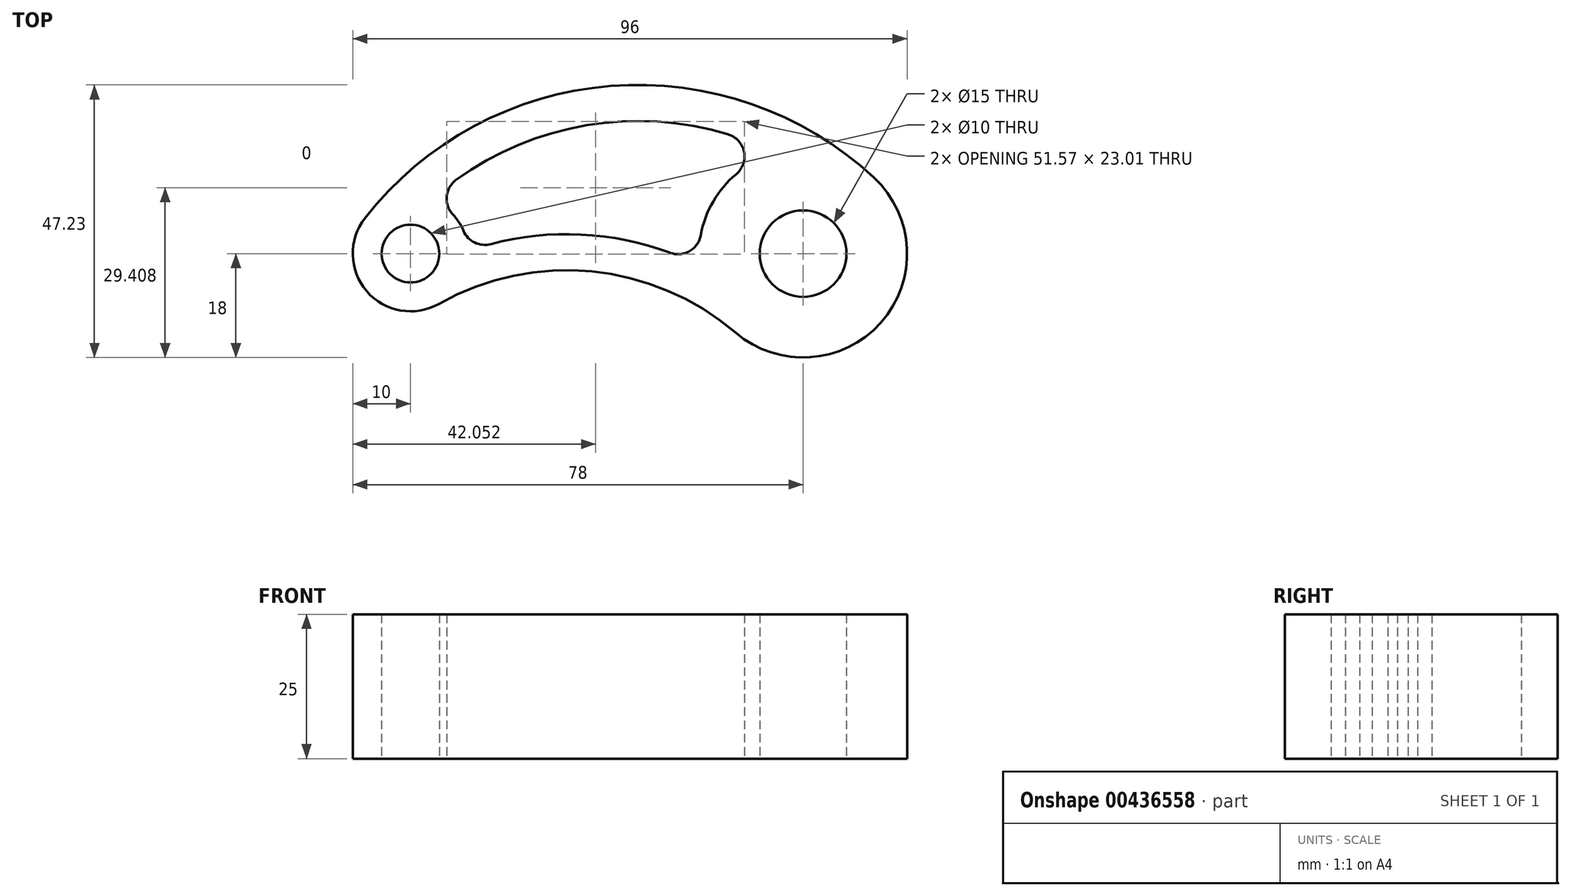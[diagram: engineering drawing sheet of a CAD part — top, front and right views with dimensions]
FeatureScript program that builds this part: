
annotation { "Feature Type Name" : "Feature", "Feature Type Description" : "" }
export const myFeature = defineFeature(function(context is Context, id is Id, definition is map)
    precondition{}
    {
        {
            var Q0;
            Q0=qCreatedBy(makeId("Top.planeOp"),FACE);
            var sketch = newSketch(context, id + "F0", { "sketchPlane" : qUnion([Q0])});
            skCircle(sketch, "E0", {"center": v(68, 0) * mm, "radius": 7.5 * mm});
            skArc(sketch, "E1", {"start": v(80.25, 13.19) * mm, "mid": v(81.44, -11.98) * mm, "end": v(56.3, -13.68) * mm});
            skCircle(sketch, "E2", {"center": v(0, 0) * mm, "radius": 5 * mm});
            skArc(sketch, "E3", {"start": v(-7.88, 6.15) * mm, "mid": v(-7.58, -6.53) * mm, "end": v(4.92, -8.7) * mm});
            skArc(sketch, "E4", {"start": v(56.3, -13.68) * mm, "mid": v(31.4, -3.1) * mm, "end": v(4.92, -8.7) * mm});
            skArc(sketch, "E5", {"start": v(80.25, 13.19) * mm, "mid": v(34.64, 29.04) * mm, "end": v(-7.88, 6.15) * mm});
            skArc(sketch, "E6", {"start": v(13.9, 1.65) * mm, "mid": v(29.54, 3.3) * mm, "end": v(44.95, 0.14) * mm});
            skArc(sketch, "E7", {"start": v(7.9, 12.78) * mm, "mid": v(30.53, 22.24) * mm, "end": v(55, 20.67) * mm});
            skArc(sketch, "E8", {"start": v(7.32, 6.81) * mm, "mid": v(8.38, 5.46) * mm, "end": v(9.2, 3.94) * mm});
            skArc(sketch, "E9", {"start": v(56.42, 13.78) * mm, "mid": v(52.42, 9.02) * mm, "end": v(50.28, 3.18) * mm});
            skPoint(sketch, "E10.visualSharp", {"position": v(10, 0.44) * mm});
            skArc(sketch, "E10.filletArc", {"start": v(9.2, 3.94) * mm, "mid": v(11.12, 1.92) * mm, "end": v(13.9, 1.65) * mm});
            skPoint(sketch, "E11.visualSharp", {"position": v(3.61, 9.32) * mm});
            skArc(sketch, "E11.filletArc", {"start": v(7.9, 12.78) * mm, "mid": v(6.27, 9.93) * mm, "end": v(7.32, 6.81) * mm});
            skPoint(sketch, "E12.visualSharp", {"position": v(63.3, 17.38) * mm});
            skArc(sketch, "E12.filletArc", {"start": v(56.42, 13.78) * mm, "mid": v(57.76, 17.65) * mm, "end": v(55, 20.67) * mm});
            skPoint(sketch, "E13.visualSharp", {"position": v(50.12, -2.12) * mm});
            skArc(sketch, "E13.filletArc", {"start": v(44.95, 0.14) * mm, "mid": v(48.33, 0.42) * mm, "end": v(50.28, 3.18) * mm});
            skSolve(sketch);
        }
        {
            var Q0;
            Q0=makeQuery(id+"F0.imprint","IMPRINT",FACE,{"disambiguationData":[TD([[makeQuery(id+"F0.imprint","IMPRINT",EDGE,{"derivedFrom":sQuery(id+"F0.wireOp",EDGE,"E0")}),-1.0]])]});
            extrude(context, id + "F1", {"entities" : qUnion([Q0]), "depth" : 25 * mm});
        }
    });
